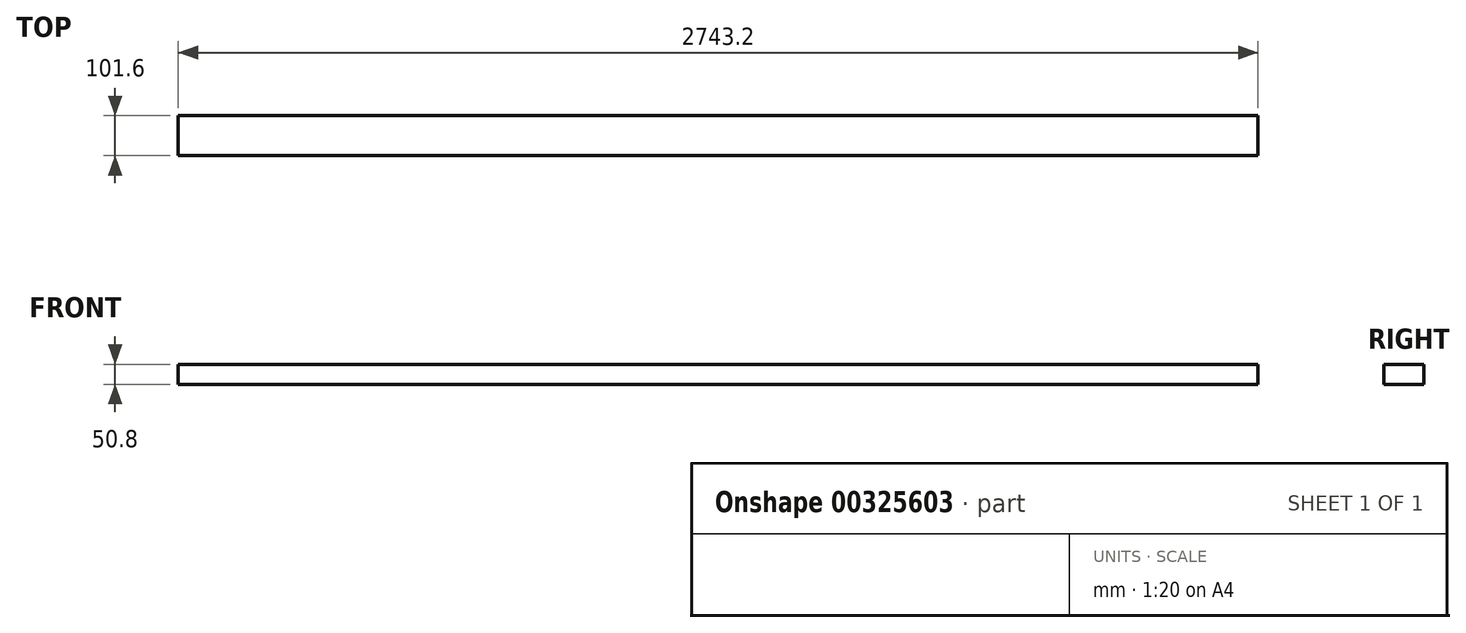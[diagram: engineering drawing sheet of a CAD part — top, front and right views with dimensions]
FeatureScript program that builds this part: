
annotation { "Feature Type Name" : "Feature", "Feature Type Description" : "" }
export const myFeature = defineFeature(function(context is Context, id is Id, definition is map)
    precondition{}
    {
        {
            var Q0;
            Q0=qCreatedBy(makeId("Top.planeOp"),FACE);
            var sketch = newSketch(context, id + "F0", { "sketchPlane" : qUnion([Q0])});
            skLineSegment(sketch, "E0.bottom", {"start": v(-298.2, 15.85) * mm, "end": v(2445, 15.85) * mm});
            skLineSegment(sketch, "E0.top", {"start": v(-298.2, -85.75) * mm, "end": v(2445, -85.75) * mm});
            skLineSegment(sketch, "E0.left", {"start": v(-298.2, 15.85) * mm, "end": v(-298.2, -85.75) * mm});
            skLineSegment(sketch, "E0.right", {"start": v(2445, 15.85) * mm, "end": v(2445, -85.75) * mm});
            skSolve(sketch);
        }
        {
            var Q0;
            Q0 = qSketchRegion(id + "F0", true);
            var Q1;
            Q1=makeQuery(id+"F0.imprint","IMPRINT",FACE,{"disambiguationData":[TD([[makeQuery(id+"F0.imprint","IMPRINT",EDGE,{"derivedFrom":sQuery(id+"F0.wireOp",EDGE,"E0.bottom")}),-1.0]])]});
            extrude(context, id + "F1", {"entities" : qUnion([Q0, Q1]), "depth" : 50.8 * mm});
        }
    });
